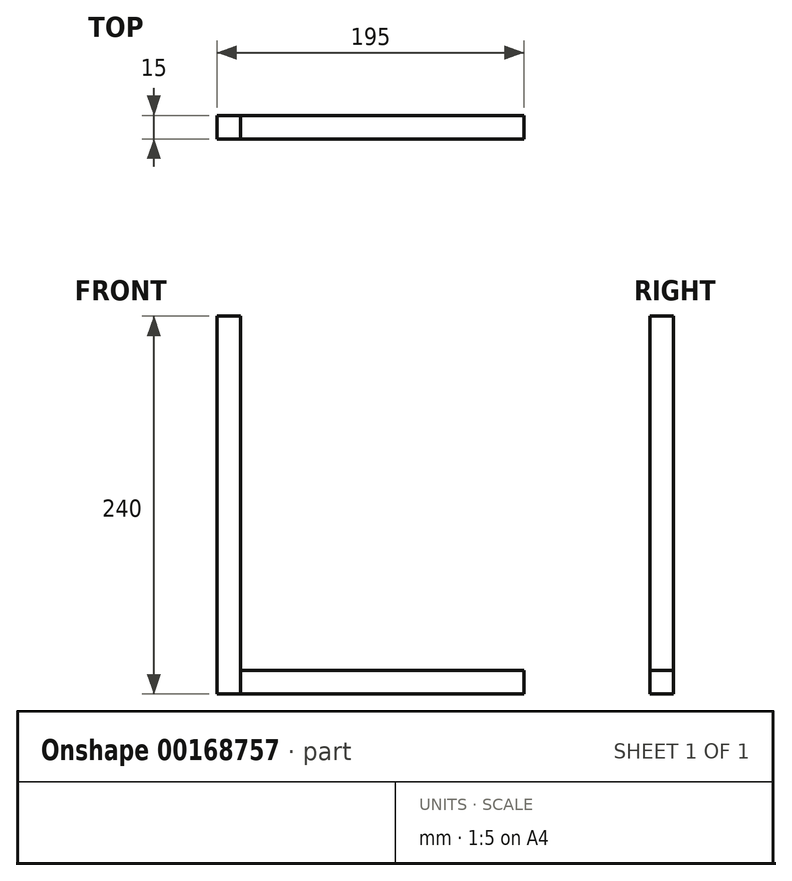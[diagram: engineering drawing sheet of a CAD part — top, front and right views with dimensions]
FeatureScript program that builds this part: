
annotation { "Feature Type Name" : "Feature", "Feature Type Description" : "" }
export const myFeature = defineFeature(function(context is Context, id is Id, definition is map)
    precondition{}
    {
        {
            var Q0;
            Q0=qCreatedBy(makeId("Top.planeOp"),FACE);
            var sketch = newSketch(context, id + "F0", { "sketchPlane" : qUnion([Q0])});
            skLineSegment(sketch, "E0.bottom", {"start": v(7.5, 7.5) * mm, "end": v(-7.5, 7.5) * mm});
            skLineSegment(sketch, "E0.top", {"start": v(7.5, -7.5) * mm, "end": v(-7.5, -7.5) * mm});
            skLineSegment(sketch, "E0.left", {"start": v(7.5, 7.5) * mm, "end": v(7.5, -7.5) * mm});
            skLineSegment(sketch, "E0.right", {"start": v(-7.5, 7.5) * mm, "end": v(-7.5, -7.5) * mm});
            skPoint(sketch, "E0.middle", {"position": v(0, 0) * mm});
            skSolve(sketch);
        }
        {
            var Q0;
            Q0 = qSketchRegion(id + "F0", true);
            extrude(context, id + "F3", {"entities" : qUnion([Q0]), "depth" : 240 * mm});
        }
        {
            var Q0;
            Q0 = qSketchRegion(id + "F0", true);
            extrude(context, id + "F1", {"entities" : qUnion([Q0]), "depth" : 180 * mm});
        }
        {
            var Q0;
            Q0=makeQuery(id+"F1.opExtrude","SWEPT_BODY",BODY,{"disambiguationData":[OSD([sQuery(id+"F0.wireOp",EDGE,"E0.bottom"),sQuery(id+"F0.wireOp",EDGE,"E0.top"),sQuery(id+"F0.wireOp",EDGE,"E0.left"),sQuery(id+"F0.wireOp",EDGE,"E0.right")])]});
            var Q1;
            Q1=sQuery(id+"F0.wireOp",EDGE,"E0.left");
            transform(context, id + "F2", {"entities" : qUnion([Q0]), "transformType" : TransformType.ROTATION, "transformAxis" : qUnion([Q1]), "angle" : 90 * degree, "oppositeDirection" : true, "makeCopy" : false});
        }
    });
